# Revit family: Access_Door-Lightweight-Best Access Doors-Insulated-BA-ALI
name_source: partatom
category: Specialty Equipment
revit_build: Autodesk Revit 2017 (Build: 20160225_1515(x64)
units: mm (PartAtom-declared; Revit-internal decimal feet)

## family parameters
Cut with Voids When Loaded = No
Host = Face
OmniClass Number = 23.30.10.27.17
Part Type = Normal
Room Calculation Point = No
Round Connector Dimension = Use Diameter
Shared = No

## types (7) — shared parameters
Assembly Code = C1020700
Construction Material = Metal - Best Access Doors - Aluminum
Default Elevation = 0"
Description = BA-ALI - Insulated Aluminum Access Door
Finish = Metal - Best Access Doors - Powder Coated White
Frame Depth = 2 7/16"
Manufacturer = Best Access Doors
Model = BA-ALI
Neoprene Gasket = Neoprene - Best Access Doors -  Gasket
Product data url = https://bimobject.com
URL = https://www.bestaccessdoors.com

## per-type parameters (varying)
| type | Door Height | Door Height Calc | Door Width | Door Width Calc | Height Actual | Width Actual |
| Custom | 24" | 24" | 24" | 24" | 26" | 26" |
| 8 x 8 | 8" | 8" | 8" | 8" | 10" | 10" |
| 12 x 12 | 12" | 12" | 12" | 12" | 14" | 14" |
| 16 x 16 | 16" | 16" | 16" | 16" | 18" | 18" |
| 18 x 18 | 18" | 18" | 18" | 18" | 20" | 20" |
| 24 x 24 | 24" | 24" | 24" | 24" | 26" | 26" |
| 36 x 36 | 36" | 36" | 36" | 36" | 38" | 38" |

## geometry (parser evidence)
native form markers: Blend x2, Sweep x14
no freeform markers — native parametric forms only
